# Revit family: AE21
name_source: partatom
category: Lighting Fixtures
revit_build: Autodesk Revit 2014 (Build: 20130308_1515(x64)
units: mm (PartAtom-declared; Revit-internal decimal feet)

## types (5) — shared parameters
Apparent Load = 65 VA
Assembly Code = D5020200
Color Filter = 16777215
Description = Site/Roadway Luminaire
Dimming Lamp Color Temperature Shift = <None>
Emit Shape Visible in Rendering = No
Emit from Circle Diameter = 24"
Finish = All colors shall be a Super TGIC powder coat paint. Optional white (WH) and custom colors available.
Glass Material = Glass-Kim Lighting-Clear
Housing Material = Metal-Kim Lighting-Aluminum Alloy
Inside Material = Metal-Kim Lighting-Aluminum-Reflective
Lamp = LED Array
Load Classification = Lighting
Manufacturer = Beacon
MasterFormat Title = Parking Lighting, Roadway Lighting, Site Lighting
Model = Acorns
Number of Poles = 1
OmniClass Number = 23-80 70 14 21
OmniClass Title = Street and Roadway Lighting
Photometric Notes = More IES files download on Photometric Web Link
Photometric Web File = generic
Power Factor = 1
Product Documentation Link = https://hubbellcdn.com
Product Page URL = https://www.hubbell.com
Revision Date = 08/29/2019
Series = Acorns
Tilt Angle = 60.00°
Type Comments = Lighting Fixture
URL = https://www.hubbell.com
Voltage = 120 V
Wattage Comments = 65 W

## per-type parameters (varying)
| type | Base Height | Base of Fixture | Fitter | Mount Height | Pole Finish | Pole Height |
| 2A24-H1 | 182" | 10" | Base : H1 | 192" | Metal-Kim Lighting-Aluminum Alloy | 176 7/8" |
| 2A24-H2 | 178" | 14" | Base : H2 | 192" | Metal-Kim Lighting-Aluminum Alloy | 176 7/8" |
| 2A24-H3 | 182" | 10" | Base : H3 | 192" | Metal-Kim Lighting-Aluminum Alloy | 176 7/8" |
| 2A24-F13 | 142 1/2" | 7 1/2" | Base : F13 | 150" | Metal-Lighting-Aluminum Alloy | 134 7/8" |
| 2A24-F21 | 180" | 12" | Base : F21 | 192" | Metal-Kim Lighting-Aluminum Alloy | 176 7/8" |

## geometry (parser evidence)
native form markers: Blend x6, Sweep x10
no freeform markers — native parametric forms only
